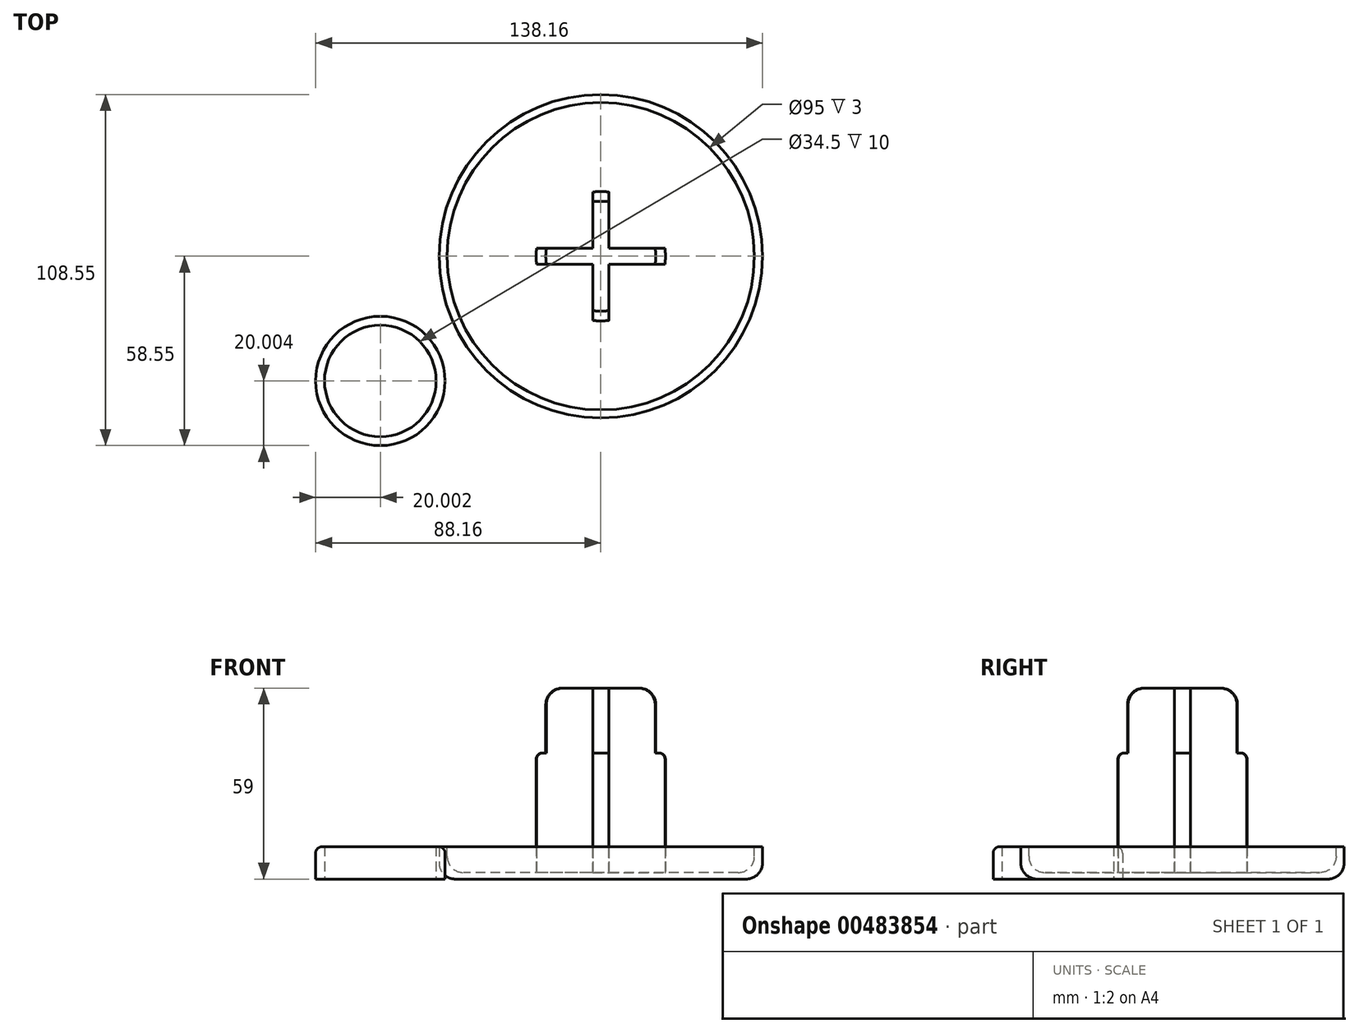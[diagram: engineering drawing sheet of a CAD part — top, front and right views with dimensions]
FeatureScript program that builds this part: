
annotation { "Feature Type Name" : "Feature", "Feature Type Description" : "" }
export const myFeature = defineFeature(function(context is Context, id is Id, definition is map)
    precondition{}
    {
        {
            var Q0;
            Q0=qCreatedBy(makeId("Top.planeOp"),FACE);
            var sketch = newSketch(context, id + "F0", { "sketchPlane" : qUnion([Q0])});
            skCircle(sketch, "E0", {"center": v(0, 0) * mm, "radius": 50 * mm});
            skSolve(sketch);
        }
        {
            var Q0;
            Q0 = qSketchRegion(id + "F0", true);
            extrude(context, id + "F1", {"entities" : qUnion([Q0]), "depth" : 10 * mm});
        }
        {
            var Q0;
            Q0=makeQuery(id+"F1.opExtrude","CAP_FACE",FACE,{"disambiguationData":[OSD([sQuery(id+"F0.wireOp",EDGE,"E0")])],"isStart":false});
            var sketch = newSketch(context, id + "F2", { "sketchPlane" : qUnion([Q0])});
            skCircle(sketch, "E1", {"center": v(0, 0) * mm, "radius": 47.5 * mm});
            skSolve(sketch);
        }
        {
            var Q0;
            Q0 = qSketchRegion(id + "F2", true);
            extrude(context, id + "F3", {"entities" : qUnion([Q0]), "operationType" : NewBodyOperationType.REMOVE, "oppositeDirection" : true, "depth" : 8 * mm});
        }
        {
            var Q0;
            Q0=makeQuery(id+"F1.opExtrude","CAP_EDGE",EDGE,{"disambiguationData":[OSD([sQuery(id+"F0.wireOp",EDGE,"E0")])],"isStart":true});
            var Q1;
            Q1=makeQuery(id+"F3.boolean.opBoolean","COPY",EDGE,{"derivedFrom":makeQuery(id+"F3.opExtrude","CAP_EDGE",EDGE,{"disambiguationData":[OSD([sQuery(id+"F2.wireOp",EDGE,"E1")])],"isStart":false})});
            fillet(context, id + "F4", {"entities" : qUnion([Q0, Q1]), "radius" : 5 * mm, "tangentPropagation" : true, "allowEdgeOverflow" : false});
        }
        {
            var Q0;
            Q0=makeQuery(id+"F3.boolean.opBoolean","COPY",FACE,{"derivedFrom":makeQuery(id+"F3.opExtrude","CAP_FACE",FACE,{"disambiguationData":[OSD([sQuery(id+"F2.wireOp",EDGE,"E1")])],"isStart":false})});
            var sketch = newSketch(context, id + "F5", { "sketchPlane" : qUnion([Q0])});
            skCircle(sketch, "E2", {"center": v(0, 0) * mm, "radius": 20 * mm});
            skSolve(sketch);
        }
        {
            var Q0;
            Q0 = qSketchRegion(id + "F5", true);
            extrude(context, id + "F6", {"entities" : qUnion([Q0]), "operationType" : NewBodyOperationType.ADD, "depth" : 37 * mm});
        }
        {
            var Q0;
            Q0=makeQuery(id+"F6.opExtrude","CAP_FACE",FACE,{"disambiguationData":[OSD([sQuery(id+"F5.wireOp",EDGE,"E2")])],"isStart":false});
            var sketch = newSketch(context, id + "F7", { "sketchPlane" : qUnion([Q0])});
            skCircle(sketch, "E3", {"center": v(0, 0) * mm, "radius": 17 * mm});
            skSolve(sketch);
        }
        {
            var Q0;
            Q0 = qSketchRegion(id + "F7", true);
            extrude(context, id + "F8", {"entities" : qUnion([Q0]), "operationType" : NewBodyOperationType.ADD, "depth" : 20 * mm});
        }
        {
            var Q0;
            Q0=makeQuery(id+"F8.opExtrude","CAP_FACE",FACE,{"disambiguationData":[OSD([sQuery(id+"F7.wireOp",EDGE,"E3")])],"isStart":false});
            var sketch = newSketch(context, id + "F9", { "sketchPlane" : qUnion([Q0])});
            skLineSegment(sketch, "E4.bottom", {"start": v(-2.5, 2.5) * mm, "end": v(-28.92, 2.5) * mm});
            skLineSegment(sketch, "E4.top", {"start": v(-2.5, 27.6) * mm, "end": v(-28.92, 27.6) * mm});
            skLineSegment(sketch, "E4.left", {"start": v(-2.5, 2.5) * mm, "end": v(-2.5, 27.6) * mm});
            skLineSegment(sketch, "E4.right", {"start": v(-28.92, 2.5) * mm, "end": v(-28.92, 27.6) * mm});
            skLineSegment(sketch, "E5.bottom", {"start": v(2.5, 2.5) * mm, "end": v(26.85, 2.5) * mm});
            skLineSegment(sketch, "E5.top", {"start": v(2.5, 27.6) * mm, "end": v(26.85, 27.6) * mm});
            skLineSegment(sketch, "E5.left", {"start": v(2.5, 2.5) * mm, "end": v(2.5, 27.6) * mm});
            skLineSegment(sketch, "E5.right", {"start": v(26.85, 2.5) * mm, "end": v(26.85, 27.6) * mm});
            skLineSegment(sketch, "E6.bottom", {"start": v(2.5, -2.5) * mm, "end": v(27.7, -2.5) * mm});
            skLineSegment(sketch, "E6.top", {"start": v(2.5, -24.23) * mm, "end": v(27.7, -24.23) * mm});
            skLineSegment(sketch, "E6.left", {"start": v(2.5, -2.5) * mm, "end": v(2.5, -24.23) * mm});
            skLineSegment(sketch, "E6.right", {"start": v(27.7, -2.5) * mm, "end": v(27.7, -24.23) * mm});
            skLineSegment(sketch, "E7.bottom", {"start": v(-2.5, -2.5) * mm, "end": v(-28.06, -2.5) * mm});
            skLineSegment(sketch, "E7.top", {"start": v(-2.5, -25.87) * mm, "end": v(-28.06, -25.87) * mm});
            skLineSegment(sketch, "E7.left", {"start": v(-2.5, -2.5) * mm, "end": v(-2.5, -25.87) * mm});
            skLineSegment(sketch, "E7.right", {"start": v(-28.06, -2.5) * mm, "end": v(-28.06, -25.87) * mm});
            skSolve(sketch);
        }
        {
            var Q0;
            Q0 = qSketchRegion(id + "F9", true);
            extrude(context, id + "F10", {"entities" : qUnion([Q0]), "operationType" : NewBodyOperationType.REMOVE, "oppositeDirection" : true, "depth" : 57 * mm});
        }
        {
            var Q0;
            {var subQ0=sQuery(id+"F7.wireOp",EDGE,"E3");Q0=makeQuery(id+"F10.boolean.opBoolean","SPLIT",EDGE,{"disambiguationData":[TD([makeQuery(id+"F10.opExtrude","SWEPT_FACE",FACE,{"disambiguationData":[OSD([sQuery(id+"F9.wireOp",EDGE,"E4.bottom")])]})])],"derivedFrom":makeQuery(id+"F8.opExtrude","CAP_EDGE",EDGE,{"disambiguationData":[OSD([subQ0])],"isStart":false})});}
            var Q1;
            {var subQ0=sQuery(id+"F7.wireOp",EDGE,"E3");Q1=makeQuery(id+"F10.boolean.opBoolean","SPLIT",EDGE,{"disambiguationData":[TD([makeQuery(id+"F10.opExtrude","SWEPT_FACE",FACE,{"disambiguationData":[OSD([sQuery(id+"F9.wireOp",EDGE,"E6.left")])]})])],"derivedFrom":makeQuery(id+"F8.opExtrude","CAP_EDGE",EDGE,{"disambiguationData":[OSD([subQ0])],"isStart":false})});}
            var Q2;
            {var subQ0=sQuery(id+"F7.wireOp",EDGE,"E3");Q2=makeQuery(id+"F10.boolean.opBoolean","SPLIT",EDGE,{"disambiguationData":[TD([makeQuery(id+"F10.opExtrude","SWEPT_FACE",FACE,{"disambiguationData":[OSD([sQuery(id+"F9.wireOp",EDGE,"E5.bottom")])]})])],"derivedFrom":makeQuery(id+"F8.opExtrude","CAP_EDGE",EDGE,{"disambiguationData":[OSD([subQ0])],"isStart":false})});}
            var Q3;
            {var subQ0=sQuery(id+"F7.wireOp",EDGE,"E3");Q3=makeQuery(id+"F10.boolean.opBoolean","SPLIT",EDGE,{"disambiguationData":[TD([makeQuery(id+"F10.opExtrude","SWEPT_FACE",FACE,{"disambiguationData":[OSD([sQuery(id+"F9.wireOp",EDGE,"E4.left")])]})])],"derivedFrom":makeQuery(id+"F8.opExtrude","CAP_EDGE",EDGE,{"disambiguationData":[OSD([subQ0])],"isStart":false})});}
            fillet(context, id + "F11", {"entities" : qUnion([Q0, Q1, Q2, Q3]), "radius" : 5 * mm, "tangentPropagation" : true, "allowEdgeOverflow" : false});
        }
        {
            var Q0;
            {var subQ0=sQuery(id+"F5.wireOp",EDGE,"E2");Q0=makeQuery(id+"F10.boolean.opBoolean","SPLIT",EDGE,{"disambiguationData":[TD([makeQuery(id+"F10.opExtrude","SWEPT_FACE",FACE,{"disambiguationData":[OSD([sQuery(id+"F9.wireOp",EDGE,"E4.bottom")])]})])],"derivedFrom":makeQuery(id+"F6.opExtrude","CAP_EDGE",EDGE,{"disambiguationData":[OSD([subQ0])],"isStart":false})});}
            var Q1;
            {var subQ0=sQuery(id+"F5.wireOp",EDGE,"E2");Q1=makeQuery(id+"F10.boolean.opBoolean","SPLIT",EDGE,{"disambiguationData":[TD([makeQuery(id+"F10.opExtrude","SWEPT_FACE",FACE,{"disambiguationData":[OSD([sQuery(id+"F9.wireOp",EDGE,"E6.left")])]})])],"derivedFrom":makeQuery(id+"F6.opExtrude","CAP_EDGE",EDGE,{"disambiguationData":[OSD([subQ0])],"isStart":false})});}
            var Q2;
            {var subQ0=sQuery(id+"F5.wireOp",EDGE,"E2");Q2=makeQuery(id+"F10.boolean.opBoolean","SPLIT",EDGE,{"disambiguationData":[TD([makeQuery(id+"F10.opExtrude","SWEPT_FACE",FACE,{"disambiguationData":[OSD([sQuery(id+"F9.wireOp",EDGE,"E5.bottom")])]})])],"derivedFrom":makeQuery(id+"F6.opExtrude","CAP_EDGE",EDGE,{"disambiguationData":[OSD([subQ0])],"isStart":false})});}
            var Q3;
            {var subQ0=sQuery(id+"F5.wireOp",EDGE,"E2");Q3=makeQuery(id+"F10.boolean.opBoolean","SPLIT",EDGE,{"disambiguationData":[TD([makeQuery(id+"F10.opExtrude","SWEPT_FACE",FACE,{"disambiguationData":[OSD([sQuery(id+"F9.wireOp",EDGE,"E4.left")])]})])],"derivedFrom":makeQuery(id+"F6.opExtrude","CAP_EDGE",EDGE,{"disambiguationData":[OSD([subQ0])],"isStart":false})});}
            var Q4;
            {var subQ0=sQuery(id+"F5.wireOp",EDGE,"E2");var subQ1=sQuery(id+"F9.wireOp",EDGE,"E6.left");Q4=makeQuery(id+"F10.boolean.opBoolean","SPLIT",EDGE,{"disambiguationData":[TD([makeQuery(id+"F10.opExtrude","SWEPT_FACE",FACE,{"disambiguationData":[OSD([subQ1])]})])],"derivedFrom":makeQuery(id+"F6.opExtrude","CAP_EDGE",EDGE,{"disambiguationData":[OSD([subQ0])],"isStart":true})});}
            var Q5;
            {var subQ0=sQuery(id+"F9.wireOp",EDGE,"E4.bottom");var subQ1=sQuery(id+"F5.wireOp",EDGE,"E2");Q5=makeQuery(id+"F10.boolean.opBoolean","SPLIT",EDGE,{"disambiguationData":[TD([makeQuery(id+"F10.opExtrude","SWEPT_FACE",FACE,{"disambiguationData":[OSD([subQ0])]})])],"derivedFrom":makeQuery(id+"F6.opExtrude","CAP_EDGE",EDGE,{"disambiguationData":[OSD([subQ1])],"isStart":true})});}
            var Q6;
            {var subQ0=sQuery(id+"F9.wireOp",EDGE,"E4.left");var subQ1=sQuery(id+"F5.wireOp",EDGE,"E2");Q6=makeQuery(id+"F10.boolean.opBoolean","SPLIT",EDGE,{"disambiguationData":[TD([makeQuery(id+"F10.opExtrude","SWEPT_FACE",FACE,{"disambiguationData":[OSD([subQ0])]})])],"derivedFrom":makeQuery(id+"F6.opExtrude","CAP_EDGE",EDGE,{"disambiguationData":[OSD([subQ1])],"isStart":true})});}
            var Q7;
            {var subQ0=sQuery(id+"F9.wireOp",EDGE,"E5.bottom");var subQ1=sQuery(id+"F5.wireOp",EDGE,"E2");Q7=makeQuery(id+"F10.boolean.opBoolean","SPLIT",EDGE,{"disambiguationData":[TD([makeQuery(id+"F10.opExtrude","SWEPT_FACE",FACE,{"disambiguationData":[OSD([subQ0])]})])],"derivedFrom":makeQuery(id+"F6.opExtrude","CAP_EDGE",EDGE,{"disambiguationData":[OSD([subQ1])],"isStart":true})});}
            fillet(context, id + "F12", {"entities" : qUnion([Q0, Q1, Q2, Q3, Q4, Q5, Q6, Q7]), "radius" : 2 * mm, "tangentPropagation" : true, "allowEdgeOverflow" : false});
        }
        {
            var Q0;
            Q0=qCreatedBy(makeId("Top.planeOp"),FACE);
            var sketch = newSketch(context, id + "F13", { "sketchPlane" : qUnion([Q0])});
            skCircle(sketch, "E8", {"center": v(-68.16, -38.55) * mm, "radius": 17.25 * mm});
            skCircle(sketch, "E9", {"center": v(-68.16, -38.55) * mm, "radius": 20 * mm});
            skSolve(sketch);
        }
        {
            var Q0;
            Q0 = qSketchRegion(id + "F13", true);
            extrude(context, id + "F14", {"entities" : qUnion([Q0]), "depth" : 10 * mm});
        }
        {
            var Q0;
            Q0=makeQuery(id+"F14.opExtrude","CAP_EDGE",EDGE,{"disambiguationData":[OSD([sQuery(id+"F13.wireOp",EDGE,"E9")])],"isStart":false});
            fillet(context, id + "F15", {"entities" : qUnion([Q0]), "radius" : 2 * mm, "tangentPropagation" : true, "allowEdgeOverflow" : false});
        }
    });
